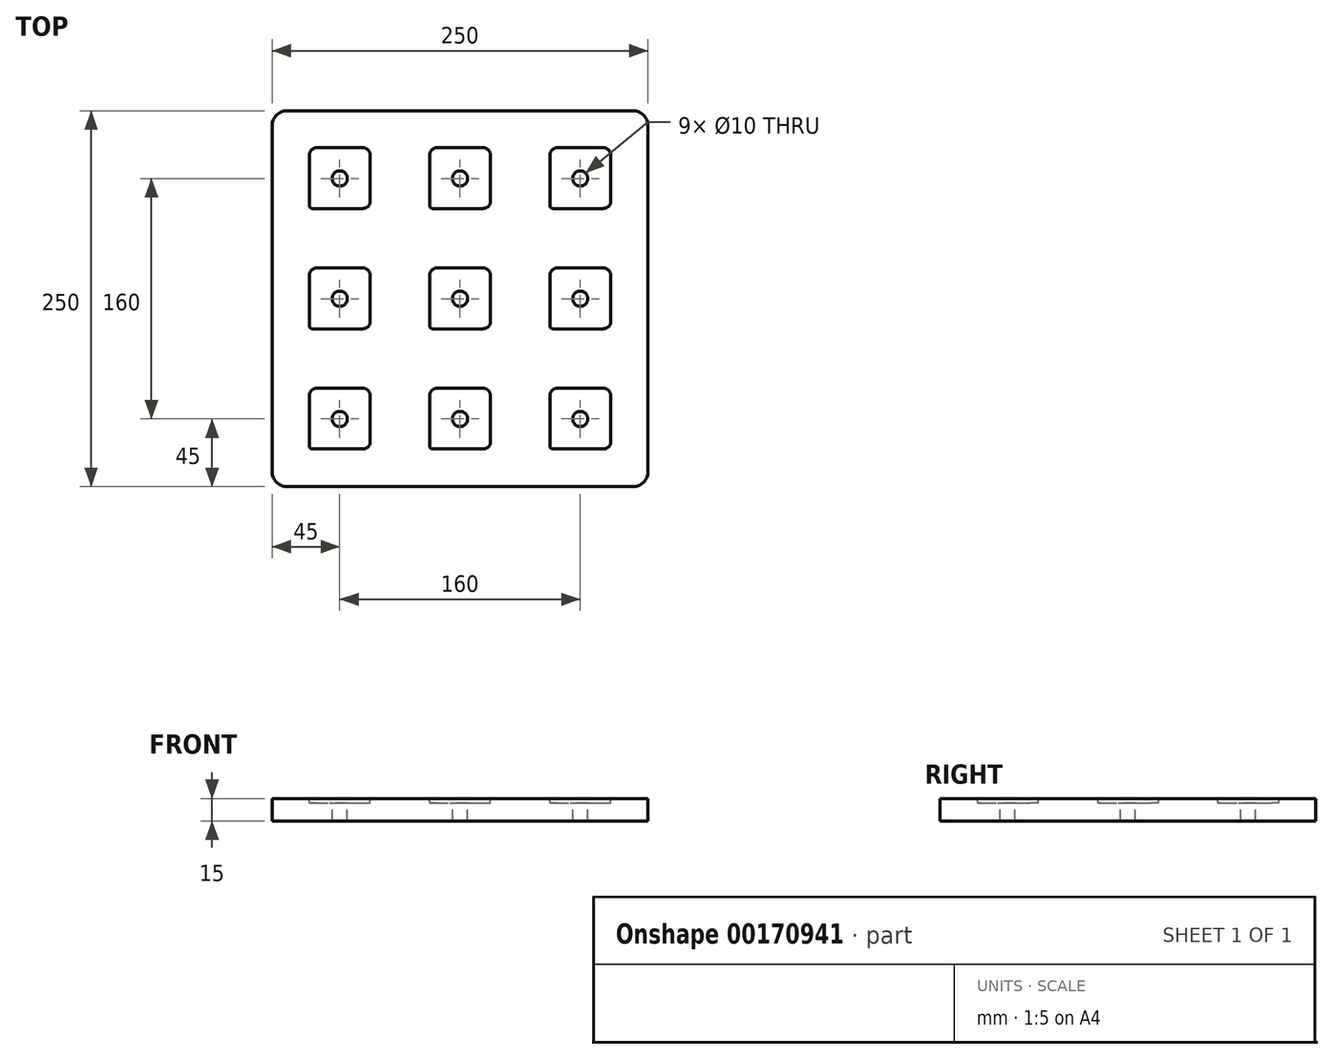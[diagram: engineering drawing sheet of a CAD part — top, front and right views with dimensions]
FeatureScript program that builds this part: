
annotation { "Feature Type Name" : "Feature", "Feature Type Description" : "" }
export const myFeature = defineFeature(function(context is Context, id is Id, definition is map)
    precondition{}
    {
        {
            var Q0;
            Q0=qCreatedBy(makeId("Top.planeOp"),FACE);
            var sketch = newSketch(context, id + "F0", { "sketchPlane" : qUnion([Q0])});
            skLineSegment(sketch, "E0.bottom", {"start": v(10, 0) * mm, "end": v(240, 0) * mm});
            skLineSegment(sketch, "E0.top", {"start": v(10, 250) * mm, "end": v(240, 250) * mm});
            skLineSegment(sketch, "E0.left", {"start": v(0, 10) * mm, "end": v(0, 240) * mm});
            skLineSegment(sketch, "E0.right", {"start": v(250, 10) * mm, "end": v(250, 240) * mm});
            skPoint(sketch, "E1", {"position": v(125, 250) * mm});
            skPoint(sketch, "E2", {"position": v(250, 125) * mm});
            skCircle(sketch, "E3", {"center": v(45, 205) * mm, "radius": 5 * mm});
            skCircle(sketch, "E4.0.1.0", {"center": v(45, 125) * mm, "radius": 5 * mm});
            skCircle(sketch, "E4.0.2.0", {"center": v(45, 45) * mm, "radius": 5 * mm});
            skCircle(sketch, "E4.1.0.0", {"center": v(125, 205) * mm, "radius": 5 * mm});
            skCircle(sketch, "E4.1.1.0", {"center": v(125, 125) * mm, "radius": 5 * mm});
            skCircle(sketch, "E4.1.2.0", {"center": v(125, 45) * mm, "radius": 5 * mm});
            skCircle(sketch, "E4.2.0.0", {"center": v(205, 205) * mm, "radius": 5 * mm});
            skCircle(sketch, "E4.2.1.0", {"center": v(205, 125) * mm, "radius": 5 * mm});
            skCircle(sketch, "E4.2.2.0", {"center": v(205, 45) * mm, "radius": 5 * mm});
            skLineSegment(sketch, "E4.direction1", {"start": v(45, 205) * mm, "end": v(125, 205) * mm, "construction": true});
            skLineSegment(sketch, "E4.direction2", {"start": v(45, 205) * mm, "end": v(45, 125) * mm, "construction": true});
            skLineSegment(sketch, "E5.bottom", {"start": v(186.75, 25) * mm, "end": v(220.25, 25) * mm});
            skLineSegment(sketch, "E5.top", {"start": v(189.75, 65.5) * mm, "end": v(220.25, 65.5) * mm});
            skLineSegment(sketch, "E5.left", {"start": v(184.75, 27) * mm, "end": v(184.75, 60.5) * mm});
            skLineSegment(sketch, "E5.right", {"start": v(225.25, 30) * mm, "end": v(225.25, 60.5) * mm});
            skPoint(sketch, "E6.visualSharp", {"position": v(184.75, 25) * mm});
            skArc(sketch, "E6.filletArc", {"start": v(184.75, 27) * mm, "mid": v(185.34, 25.59) * mm, "end": v(186.75, 25) * mm});
            skPoint(sketch, "E7.visualSharp", {"position": v(184.75, 65.5) * mm});
            skArc(sketch, "E7.filletArc", {"start": v(189.75, 65.5) * mm, "mid": v(186.21, 64.04) * mm, "end": v(184.75, 60.5) * mm});
            skPoint(sketch, "E8.visualSharp", {"position": v(225.25, 65.5) * mm});
            skArc(sketch, "E8.filletArc", {"start": v(225.25, 60.5) * mm, "mid": v(223.79, 64.04) * mm, "end": v(220.25, 65.5) * mm});
            skPoint(sketch, "E9.visualSharp", {"position": v(225.25, 25) * mm});
            skArc(sketch, "E9.filletArc", {"start": v(220.25, 25) * mm, "mid": v(223.79, 26.46) * mm, "end": v(225.25, 30) * mm});
            skLineSegment(sketch, "E10.0.1.0", {"start": v(189.75, 145.5) * mm, "end": v(220.25, 145.5) * mm});
            skArc(sketch, "E10.0.1.1", {"start": v(189.75, 145.5) * mm, "mid": v(186.21, 144.04) * mm, "end": v(184.75, 140.5) * mm});
            skLineSegment(sketch, "E10.0.1.2", {"start": v(184.75, 107) * mm, "end": v(184.75, 140.5) * mm});
            skPoint(sketch, "E10.0.1.3", {"position": v(184.75, 105) * mm});
            skArc(sketch, "E10.0.1.4", {"start": v(184.75, 107) * mm, "mid": v(185.34, 105.59) * mm, "end": v(186.75, 105) * mm});
            skLineSegment(sketch, "E10.0.1.5", {"start": v(186.75, 105) * mm, "end": v(220.25, 105) * mm});
            skArc(sketch, "E10.0.1.6", {"start": v(220.25, 105) * mm, "mid": v(223.79, 106.46) * mm, "end": v(225.25, 110) * mm});
            skLineSegment(sketch, "E10.0.1.7", {"start": v(225.25, 110) * mm, "end": v(225.25, 140.5) * mm});
            skArc(sketch, "E10.0.1.8", {"start": v(225.25, 140.5) * mm, "mid": v(223.79, 144.04) * mm, "end": v(220.25, 145.5) * mm});
            skLineSegment(sketch, "E10.0.2.0", {"start": v(189.75, 225.5) * mm, "end": v(220.25, 225.5) * mm});
            skArc(sketch, "E10.0.2.1", {"start": v(189.75, 225.5) * mm, "mid": v(186.21, 224.04) * mm, "end": v(184.75, 220.5) * mm});
            skLineSegment(sketch, "E10.0.2.2", {"start": v(184.75, 187) * mm, "end": v(184.75, 220.5) * mm});
            skPoint(sketch, "E10.0.2.3", {"position": v(184.75, 185) * mm});
            skArc(sketch, "E10.0.2.4", {"start": v(184.75, 187) * mm, "mid": v(185.34, 185.59) * mm, "end": v(186.75, 185) * mm});
            skLineSegment(sketch, "E10.0.2.5", {"start": v(186.75, 185) * mm, "end": v(220.25, 185) * mm});
            skArc(sketch, "E10.0.2.6", {"start": v(220.25, 185) * mm, "mid": v(223.79, 186.46) * mm, "end": v(225.25, 190) * mm});
            skLineSegment(sketch, "E10.0.2.7", {"start": v(225.25, 190) * mm, "end": v(225.25, 220.5) * mm});
            skArc(sketch, "E10.0.2.8", {"start": v(225.25, 220.5) * mm, "mid": v(223.79, 224.04) * mm, "end": v(220.25, 225.5) * mm});
            skLineSegment(sketch, "E10.1.0.0", {"start": v(109.75, 65.5) * mm, "end": v(140.25, 65.5) * mm});
            skArc(sketch, "E10.1.0.1", {"start": v(109.75, 65.5) * mm, "mid": v(106.21, 64.04) * mm, "end": v(104.75, 60.5) * mm});
            skLineSegment(sketch, "E10.1.0.2", {"start": v(104.75, 27) * mm, "end": v(104.75, 60.5) * mm});
            skPoint(sketch, "E10.1.0.3", {"position": v(104.75, 25) * mm});
            skArc(sketch, "E10.1.0.4", {"start": v(104.75, 27) * mm, "mid": v(105.34, 25.59) * mm, "end": v(106.75, 25) * mm});
            skLineSegment(sketch, "E10.1.0.5", {"start": v(106.75, 25) * mm, "end": v(140.25, 25) * mm});
            skArc(sketch, "E10.1.0.6", {"start": v(140.25, 25) * mm, "mid": v(143.79, 26.46) * mm, "end": v(145.25, 30) * mm});
            skLineSegment(sketch, "E10.1.0.7", {"start": v(145.25, 30) * mm, "end": v(145.25, 60.5) * mm});
            skArc(sketch, "E10.1.0.8", {"start": v(145.25, 60.5) * mm, "mid": v(143.79, 64.04) * mm, "end": v(140.25, 65.5) * mm});
            skLineSegment(sketch, "E10.1.1.0", {"start": v(109.75, 145.5) * mm, "end": v(140.25, 145.5) * mm});
            skArc(sketch, "E10.1.1.1", {"start": v(109.75, 145.5) * mm, "mid": v(106.21, 144.04) * mm, "end": v(104.75, 140.5) * mm});
            skLineSegment(sketch, "E10.1.1.2", {"start": v(104.75, 107) * mm, "end": v(104.75, 140.5) * mm});
            skPoint(sketch, "E10.1.1.3", {"position": v(104.75, 105) * mm});
            skArc(sketch, "E10.1.1.4", {"start": v(104.75, 107) * mm, "mid": v(105.34, 105.59) * mm, "end": v(106.75, 105) * mm});
            skLineSegment(sketch, "E10.1.1.5", {"start": v(106.75, 105) * mm, "end": v(140.25, 105) * mm});
            skArc(sketch, "E10.1.1.6", {"start": v(140.25, 105) * mm, "mid": v(143.79, 106.46) * mm, "end": v(145.25, 110) * mm});
            skLineSegment(sketch, "E10.1.1.7", {"start": v(145.25, 110) * mm, "end": v(145.25, 140.5) * mm});
            skArc(sketch, "E10.1.1.8", {"start": v(145.25, 140.5) * mm, "mid": v(143.79, 144.04) * mm, "end": v(140.25, 145.5) * mm});
            skLineSegment(sketch, "E10.1.2.0", {"start": v(109.75, 225.5) * mm, "end": v(140.25, 225.5) * mm});
            skArc(sketch, "E10.1.2.1", {"start": v(109.75, 225.5) * mm, "mid": v(106.21, 224.04) * mm, "end": v(104.75, 220.5) * mm});
            skLineSegment(sketch, "E10.1.2.2", {"start": v(104.75, 187) * mm, "end": v(104.75, 220.5) * mm});
            skPoint(sketch, "E10.1.2.3", {"position": v(104.75, 185) * mm});
            skArc(sketch, "E10.1.2.4", {"start": v(104.75, 187) * mm, "mid": v(105.34, 185.59) * mm, "end": v(106.75, 185) * mm});
            skLineSegment(sketch, "E10.1.2.5", {"start": v(106.75, 185) * mm, "end": v(140.25, 185) * mm});
            skArc(sketch, "E10.1.2.6", {"start": v(140.25, 185) * mm, "mid": v(143.79, 186.46) * mm, "end": v(145.25, 190) * mm});
            skLineSegment(sketch, "E10.1.2.7", {"start": v(145.25, 190) * mm, "end": v(145.25, 220.5) * mm});
            skArc(sketch, "E10.1.2.8", {"start": v(145.25, 220.5) * mm, "mid": v(143.79, 224.04) * mm, "end": v(140.25, 225.5) * mm});
            skLineSegment(sketch, "E10.2.0.0", {"start": v(29.75, 65.5) * mm, "end": v(60.25, 65.5) * mm});
            skArc(sketch, "E10.2.0.1", {"start": v(29.75, 65.5) * mm, "mid": v(26.21, 64.04) * mm, "end": v(24.75, 60.5) * mm});
            skLineSegment(sketch, "E10.2.0.2", {"start": v(24.75, 27) * mm, "end": v(24.75, 60.5) * mm});
            skPoint(sketch, "E10.2.0.3", {"position": v(24.75, 25) * mm});
            skArc(sketch, "E10.2.0.4", {"start": v(24.75, 27) * mm, "mid": v(25.34, 25.59) * mm, "end": v(26.75, 25) * mm});
            skLineSegment(sketch, "E10.2.0.5", {"start": v(26.75, 25) * mm, "end": v(60.25, 25) * mm});
            skArc(sketch, "E10.2.0.6", {"start": v(60.25, 25) * mm, "mid": v(63.79, 26.46) * mm, "end": v(65.25, 30) * mm});
            skLineSegment(sketch, "E10.2.0.7", {"start": v(65.25, 30) * mm, "end": v(65.25, 60.5) * mm});
            skArc(sketch, "E10.2.0.8", {"start": v(65.25, 60.5) * mm, "mid": v(63.79, 64.04) * mm, "end": v(60.25, 65.5) * mm});
            skLineSegment(sketch, "E10.2.1.0", {"start": v(29.75, 145.5) * mm, "end": v(60.25, 145.5) * mm});
            skArc(sketch, "E10.2.1.1", {"start": v(29.75, 145.5) * mm, "mid": v(26.21, 144.04) * mm, "end": v(24.75, 140.5) * mm});
            skLineSegment(sketch, "E10.2.1.2", {"start": v(24.75, 107) * mm, "end": v(24.75, 140.5) * mm});
            skPoint(sketch, "E10.2.1.3", {"position": v(24.75, 105) * mm});
            skArc(sketch, "E10.2.1.4", {"start": v(24.75, 107) * mm, "mid": v(25.34, 105.59) * mm, "end": v(26.75, 105) * mm});
            skLineSegment(sketch, "E10.2.1.5", {"start": v(26.75, 105) * mm, "end": v(60.25, 105) * mm});
            skArc(sketch, "E10.2.1.6", {"start": v(60.25, 105) * mm, "mid": v(63.79, 106.46) * mm, "end": v(65.25, 110) * mm});
            skLineSegment(sketch, "E10.2.1.7", {"start": v(65.25, 110) * mm, "end": v(65.25, 140.5) * mm});
            skArc(sketch, "E10.2.1.8", {"start": v(65.25, 140.5) * mm, "mid": v(63.79, 144.04) * mm, "end": v(60.25, 145.5) * mm});
            skLineSegment(sketch, "E10.2.2.0", {"start": v(29.75, 225.5) * mm, "end": v(60.25, 225.5) * mm});
            skArc(sketch, "E10.2.2.1", {"start": v(29.75, 225.5) * mm, "mid": v(26.21, 224.04) * mm, "end": v(24.75, 220.5) * mm});
            skLineSegment(sketch, "E10.2.2.2", {"start": v(24.75, 187) * mm, "end": v(24.75, 220.5) * mm});
            skPoint(sketch, "E10.2.2.3", {"position": v(24.75, 185) * mm});
            skArc(sketch, "E10.2.2.4", {"start": v(24.75, 187) * mm, "mid": v(25.34, 185.59) * mm, "end": v(26.75, 185) * mm});
            skLineSegment(sketch, "E10.2.2.5", {"start": v(26.75, 185) * mm, "end": v(60.25, 185) * mm});
            skArc(sketch, "E10.2.2.6", {"start": v(60.25, 185) * mm, "mid": v(63.79, 186.46) * mm, "end": v(65.25, 190) * mm});
            skLineSegment(sketch, "E10.2.2.7", {"start": v(65.25, 190) * mm, "end": v(65.25, 220.5) * mm});
            skArc(sketch, "E10.2.2.8", {"start": v(65.25, 220.5) * mm, "mid": v(63.79, 224.04) * mm, "end": v(60.25, 225.5) * mm});
            skLineSegment(sketch, "E10.direction1", {"start": v(189.75, 65.5) * mm, "end": v(109.75, 65.5) * mm, "construction": true});
            skLineSegment(sketch, "E10.direction2", {"start": v(189.75, 65.5) * mm, "end": v(189.75, 145.5) * mm, "construction": true});
            skPoint(sketch, "E11.visualSharp", {"position": v(0, 250) * mm});
            skArc(sketch, "E11.filletArc", {"start": v(10, 250) * mm, "mid": v(2.93, 247.07) * mm, "end": v(0, 240) * mm});
            skPoint(sketch, "E12.visualSharp", {"position": v(250, 250) * mm});
            skArc(sketch, "E12.filletArc", {"start": v(250, 240) * mm, "mid": v(247.07, 247.07) * mm, "end": v(240, 250) * mm});
            skPoint(sketch, "E13.visualSharp", {"position": v(250, 0) * mm});
            skArc(sketch, "E13.filletArc", {"start": v(240, 0) * mm, "mid": v(247.07, 2.93) * mm, "end": v(250, 10) * mm});
            skPoint(sketch, "E14.visualSharp", {"position": v(0, 0) * mm});
            skArc(sketch, "E14.filletArc", {"start": v(0, 10) * mm, "mid": v(2.93, 2.93) * mm, "end": v(10, 0) * mm});
            skSolve(sketch);
        }
        {
            var Q0;
            Q0=makeQuery(id+"F0.imprint","IMPRINT",FACE,{"disambiguationData":[TD([[makeQuery(id+"F0.imprint","IMPRINT",EDGE,{"derivedFrom":sQuery(id+"F0.wireOp",EDGE,"E0.bottom")}),1.0]])]});
            var Q1;
            Q1=makeQuery(id+"F0.imprint","IMPRINT",FACE,{"disambiguationData":[TD([[makeQuery(id+"F0.imprint","IMPRINT",EDGE,{"derivedFrom":sQuery(id+"F0.wireOp",EDGE,"E4.1.0.0")}),-1.0]])]});
            var Q2;
            Q2=makeQuery(id+"F0.imprint","IMPRINT",FACE,{"disambiguationData":[TD([[makeQuery(id+"F0.imprint","IMPRINT",EDGE,{"derivedFrom":sQuery(id+"F0.wireOp",EDGE,"E3")}),-1.0]])]});
            var Q3;
            Q3=makeQuery(id+"F0.imprint","IMPRINT",FACE,{"disambiguationData":[TD([[makeQuery(id+"F0.imprint","IMPRINT",EDGE,{"derivedFrom":sQuery(id+"F0.wireOp",EDGE,"E4.2.0.0")}),-1.0]])]});
            var Q4;
            Q4=makeQuery(id+"F0.imprint","IMPRINT",FACE,{"disambiguationData":[TD([[makeQuery(id+"F0.imprint","IMPRINT",EDGE,{"derivedFrom":sQuery(id+"F0.wireOp",EDGE,"E4.2.1.0")}),-1.0]])]});
            var Q5;
            Q5=makeQuery(id+"F0.imprint","IMPRINT",FACE,{"disambiguationData":[TD([[makeQuery(id+"F0.imprint","IMPRINT",EDGE,{"derivedFrom":sQuery(id+"F0.wireOp",EDGE,"E4.1.1.0")}),-1.0]])]});
            var Q6;
            Q6=makeQuery(id+"F0.imprint","IMPRINT",FACE,{"disambiguationData":[TD([[makeQuery(id+"F0.imprint","IMPRINT",EDGE,{"derivedFrom":sQuery(id+"F0.wireOp",EDGE,"E4.0.1.0")}),-1.0]])]});
            var Q7;
            Q7=makeQuery(id+"F0.imprint","IMPRINT",FACE,{"disambiguationData":[TD([[makeQuery(id+"F0.imprint","IMPRINT",EDGE,{"derivedFrom":sQuery(id+"F0.wireOp",EDGE,"E4.0.2.0")}),-1.0]])]});
            var Q8;
            Q8=makeQuery(id+"F0.imprint","IMPRINT",FACE,{"disambiguationData":[TD([[makeQuery(id+"F0.imprint","IMPRINT",EDGE,{"derivedFrom":sQuery(id+"F0.wireOp",EDGE,"E4.1.2.0")}),-1.0]])]});
            var Q9;
            Q9=makeQuery(id+"F0.imprint","IMPRINT",FACE,{"disambiguationData":[TD([[makeQuery(id+"F0.imprint","IMPRINT",EDGE,{"derivedFrom":sQuery(id+"F0.wireOp",EDGE,"E4.2.2.0")}),-1.0]])]});
            extrude(context, id + "F1", {"entities" : qUnion([Q0, Q1, Q2, Q3, Q4, Q5, Q6, Q7, Q8, Q9]), "oppositeDirection" : true, "depth" : 15 * mm});
        }
        {
            var Q0;
            Q0=makeQuery(id+"F0.imprint","IMPRINT",FACE,{"disambiguationData":[TD([[makeQuery(id+"F0.imprint","IMPRINT",EDGE,{"derivedFrom":sQuery(id+"F0.wireOp",EDGE,"E3")}),-1.0]])]});
            var Q1;
            Q1=makeQuery(id+"F0.imprint","IMPRINT",FACE,{"disambiguationData":[TD([[makeQuery(id+"F0.imprint","IMPRINT",EDGE,{"derivedFrom":sQuery(id+"F0.wireOp",EDGE,"E4.0.1.0")}),-1.0]])]});
            var Q2;
            Q2=makeQuery(id+"F0.imprint","IMPRINT",FACE,{"disambiguationData":[TD([[makeQuery(id+"F0.imprint","IMPRINT",EDGE,{"derivedFrom":sQuery(id+"F0.wireOp",EDGE,"E4.0.2.0")}),-1.0]])]});
            var Q3;
            Q3=makeQuery(id+"F0.imprint","IMPRINT",FACE,{"disambiguationData":[TD([[makeQuery(id+"F0.imprint","IMPRINT",EDGE,{"derivedFrom":sQuery(id+"F0.wireOp",EDGE,"E4.1.2.0")}),-1.0]])]});
            var Q4;
            Q4=makeQuery(id+"F0.imprint","IMPRINT",FACE,{"disambiguationData":[TD([[makeQuery(id+"F0.imprint","IMPRINT",EDGE,{"derivedFrom":sQuery(id+"F0.wireOp",EDGE,"E4.1.1.0")}),-1.0]])]});
            var Q5;
            Q5=makeQuery(id+"F0.imprint","IMPRINT",FACE,{"disambiguationData":[TD([[makeQuery(id+"F0.imprint","IMPRINT",EDGE,{"derivedFrom":sQuery(id+"F0.wireOp",EDGE,"E4.1.0.0")}),-1.0]])]});
            var Q6;
            Q6=makeQuery(id+"F0.imprint","IMPRINT",FACE,{"disambiguationData":[TD([[makeQuery(id+"F0.imprint","IMPRINT",EDGE,{"derivedFrom":sQuery(id+"F0.wireOp",EDGE,"E4.2.0.0")}),-1.0]])]});
            var Q7;
            Q7=makeQuery(id+"F0.imprint","IMPRINT",FACE,{"disambiguationData":[TD([[makeQuery(id+"F0.imprint","IMPRINT",EDGE,{"derivedFrom":sQuery(id+"F0.wireOp",EDGE,"E4.2.1.0")}),-1.0]])]});
            var Q8;
            Q8=makeQuery(id+"F0.imprint","IMPRINT",FACE,{"disambiguationData":[TD([[makeQuery(id+"F0.imprint","IMPRINT",EDGE,{"derivedFrom":sQuery(id+"F0.wireOp",EDGE,"E4.2.2.0")}),-1.0]])]});
            extrude(context, id + "F2", {"entities" : qUnion([Q0, Q1, Q2, Q3, Q4, Q5, Q6, Q7, Q8]), "operationType" : NewBodyOperationType.REMOVE, "oppositeDirection" : true, "depth" : 3 * mm});
        }
    });
